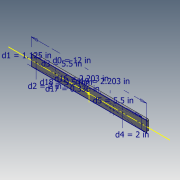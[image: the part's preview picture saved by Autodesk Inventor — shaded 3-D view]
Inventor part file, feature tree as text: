
AUTODESK INVENTOR PART (.ipt)
format: ipt  version: 2018.3 (Build 223284000, 284)  size: 123,904 bytes
history: native  units: in
note: dims shown in document units (in); Inventor stores cm internally (conversion verified against a paired STEP export)
features: hole x2, sketch x1, extrude x1, fillet x1
ambient origin geometry x8: Origin, YZ Plane, XZ Plane, XY Plane, X Axis, Y Axis, Z Axis, Center Point
bodies: Solid1 (feature_tree)
feature tree (5):
  sketch  "Sketch1"  dims[d0=12.0in d1=1.125in d2=2.0in d3=5.5in d4=2.0in d5=5.5in d6=0.22in d7=0.0in d8=0.123in d9=0.75in d10=0.375in d11=0.25in d12=0.5635in d13=1.0in d14=0.8108in d15=0.125in d16=2.203in d17=0.336in d18=0.374in d19=2.203in d20=0.06in d21=0.75in d22=0.375in d23=0.25in d24=0.5635in d25=1.0in d26=0.8108in]
  extrude  "Extrusion1"  Depth=1.125in
  hole  "Hole1-Tap M4"  [1 undecoded]
  fillet  "Fillet1"  Radius=5.5in
  hole  "Hole2-Tap M2"  [1 undecoded]
note: 2 required parameter values undecoded (feature->parameter linkage not recoverable at this tier; creation-order binding heuristic only, values carry confidence <= 0.55)
